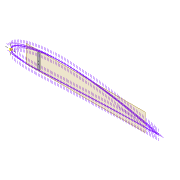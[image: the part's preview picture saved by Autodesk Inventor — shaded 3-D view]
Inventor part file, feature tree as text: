
AUTODESK INVENTOR PART (.ipt)
format: ipt  version: 2022 (Build 260153000, 153)  size: 439,808 bytes
history: native  units: mm
features: sketch x9, projected_geometry x8, extrude x7, shell x1, plane x1, chamfer x1
ambient origin geometry x8: Origin, YZ Plane, XZ Plane, XY Plane, X Axis, Y Axis, Z Axis, Center Point
bodies: Solid1 (feature_tree)
feature tree (27):
  extrude  "Extrusion1"  Depth=2.0mm
  shell  "Shell1"  Thickness=2.0mm
  extrude  "Extrusion8"  Depth=2.0mm
  extrude  "Extrusion3"  Depth=10.0mm TaperAngle=0.0deg
  extrude  "Extrusion4"  Depth=5.0mm
  extrude  "Extrusion5"  Depth=2.5mm
  plane  "Work Plane2"
  extrude  "Extrusion9"  Depth=5.0mm
  chamfer  "Chamfer1"  Distance=2.0mm
  extrude  "Extrusion10"  Depth=10.0mm
  sketch  "Sketch27"  dims[d62=65.0mm]
  sketch  "Sketch28"  dims[d63=5.0mm d64=2.0mm d65=0.0mm d66=2.5mm d67=10.0mm d68=70.0mm d69=20.0mm d70=0.5mm d71=10.0mm d72=0.0mm d73=3.0mm d74=3.0mm d75=2.0mm d76=45.0deg d77=1.0mm d78=0.0mm d79=1.0mm d80=1.0mm d82=1.0mm d83=1.0mm d84=10.0mm d85=0.0mm]
  sketch  "Sketch3"  dims[d0=2.0mm d1=0.0mm d2=4.0mm d7=2.0mm]
  sketch  "Sketch8"  dims[d8=2.0mm d9=5.9mm]
  sketch  "Sketch9"  dims[d13=10.0mm d14=0.0mm d16=10.0mm d17=0.0mm]
  sketch  "Sketch10"  dims[d22=2.0mm d23=0.0mm d32=5.0mm]
  projected_geometry  "Projected Loop4"
  projected_geometry  "Projected Loop10"
  sketch  "Sketch24"  dims[d34=1.6mm d35=2.5mm]
  projected_geometry  "Projected Loop11"
  projected_geometry  "Projected Loop12"
  sketch  "Sketch25"  dims[d37=5.0mm d38=1.6mm]
  projected_geometry  "Projected Loop13"
  sketch  "Sketch26"  dims[d40=2.5mm]
  projected_geometry  "Project Cut Edges1"
  projected_geometry  "Project Cut Edges2"
  projected_geometry  "Project Cut Edges3"
